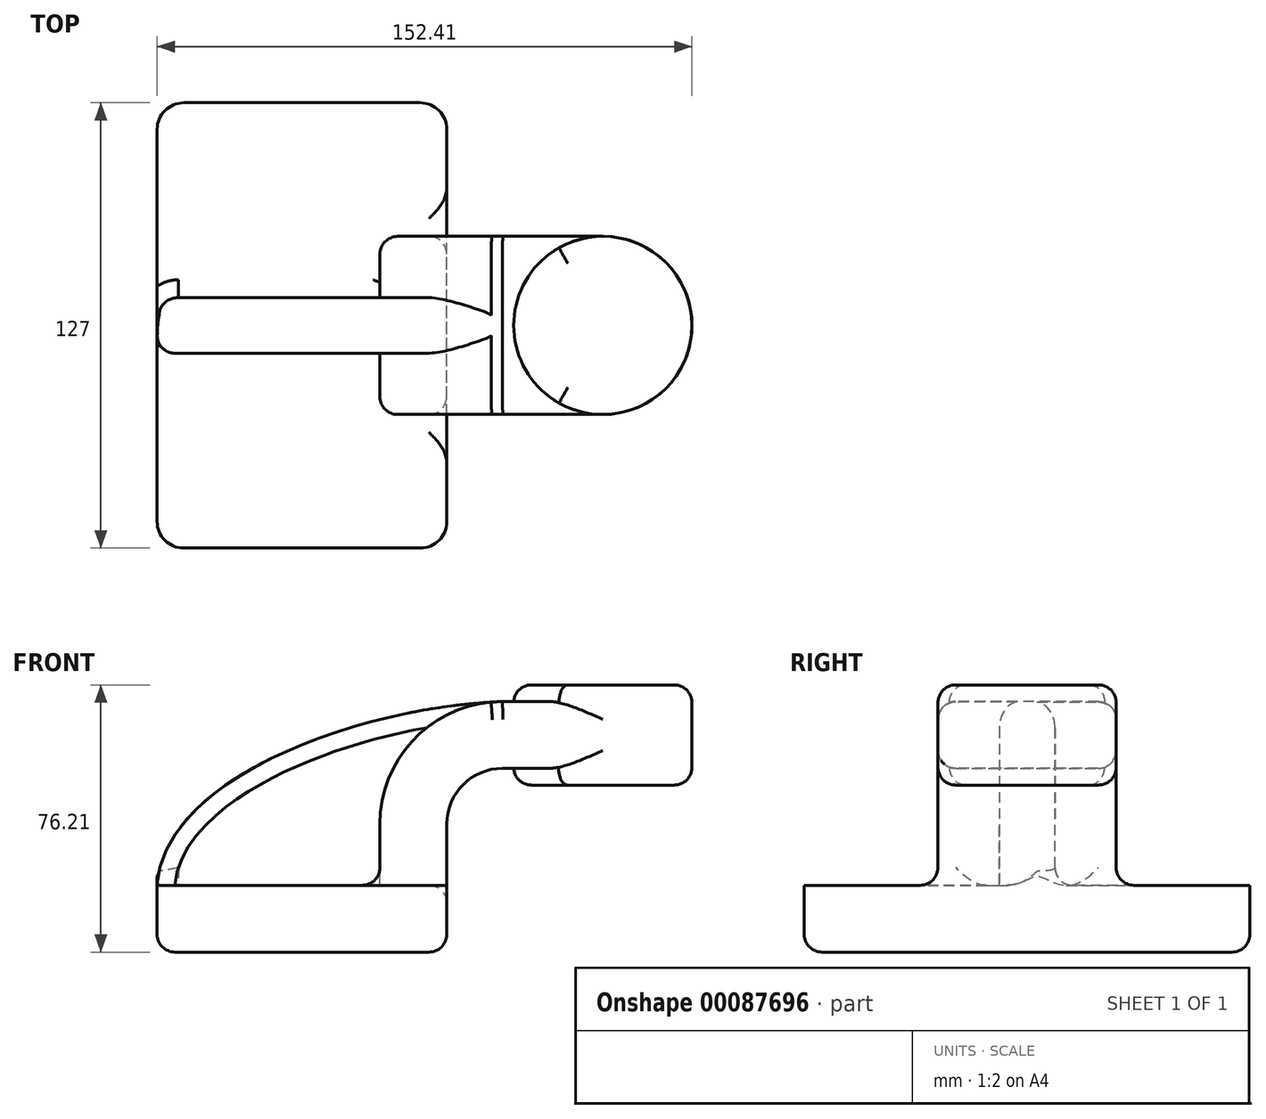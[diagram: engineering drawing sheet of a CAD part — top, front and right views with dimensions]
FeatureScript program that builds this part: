
annotation { "Feature Type Name" : "Feature", "Feature Type Description" : "" }
export const myFeature = defineFeature(function(context is Context, id is Id, definition is map)
    precondition{}
    {
        {
            var Q0;
            Q0=qCreatedBy(makeId("Front.planeOp"),FACE);
            var sketch = newSketch(context, id + "F0", { "sketchPlane" : qUnion([Q0])});
            skLineSegment(sketch, "E0.rect.bottom", {"start": v(-41.28, 9.52) * mm, "end": v(41.28, 9.52) * mm});
            skLineSegment(sketch, "E0.rect.top", {"start": v(-41.28, -9.52) * mm, "end": v(41.28, -9.52) * mm});
            skLineSegment(sketch, "E0.rect.left", {"start": v(-41.28, 9.52) * mm, "end": v(-41.28, -9.52) * mm});
            skLineSegment(sketch, "E0.rect.right", {"start": v(41.28, 9.52) * mm, "end": v(41.28, -9.52) * mm});
            skPoint(sketch, "E0.rect.middle", {"position": v(0, 0) * mm});
            skLineSegment(sketch, "E1", {"start": v(41.28, 9.52) * mm, "end": v(41.28, 27) * mm});
            skArc(sketch, "E2", {"start": v(41.28, 27) * mm, "mid": v(45.92, 38.23) * mm, "end": v(57.15, 42.88) * mm});
            skLineSegment(sketch, "E3", {"start": v(57.15, 42.88) * mm, "end": v(85.72, 42.88) * mm});
            skLineSegment(sketch, "E4.rect.bottom", {"start": v(60.32, 38.1) * mm, "end": v(111.12, 38.1) * mm});
            skLineSegment(sketch, "E4.rect.top", {"start": v(60.32, 66.68) * mm, "end": v(111.12, 66.68) * mm});
            skLineSegment(sketch, "E4.rect.left", {"start": v(60.32, 38.1) * mm, "end": v(60.32, 66.68) * mm});
            skLineSegment(sketch, "E4.rect.right", {"start": v(111.13, 38.1) * mm, "end": v(111.12, 66.68) * mm});
            skPoint(sketch, "E4.rect.middle", {"position": v(85.72, 52.39) * mm});
            skLineSegment(sketch, "E5.0", {"start": v(57.15, 61.93) * mm, "end": v(85.72, 61.93) * mm});
            skArc(sketch, "E5.1", {"start": v(22.23, 27) * mm, "mid": v(32.45, 51.7) * mm, "end": v(57.15, 61.93) * mm});
            skLineSegment(sketch, "E5.2", {"start": v(22.23, 9.52) * mm, "end": v(22.23, 27) * mm});
            skLineSegment(sketch, "E6", {"start": v(85.72, 38.1) * mm, "end": v(85.72, 66.68) * mm});
            skFitSpline(sketch, "E7", {"points": [v(-41.28, 9.53) * mm, v(57.15, 61.93) * mm], "startDerivative": vector(5.2, 92.34) * mm, "endDerivative": vector(120.92, 4.22) * mm});
            skSolve(sketch);
        }
        {
            var Q0;
            Q0=makeQuery(id+"F0.imprint","IMPRINT",FACE,{"disambiguationData":[TD([[makeQuery(id+"F0.imprint","IMPRINT",EDGE,{"derivedFrom":sQuery(id+"F0.wireOp",EDGE,"E0.rect.top")}),1.0]])]});
            extrude(context, id + "F1", {"entities" : qUnion([Q0]), "endBound" : BoundingType.SYMMETRIC, "depth" : 127 * mm});
        }
        {
            var Q0;
            {var subQ9=sQuery(id+"F0.wireOp",EDGE,"E1");Q0=makeQuery(id+"F0.imprint","IMPRINT",FACE,{"disambiguationData":[TD([[makeQuery(id+"F0.imprint","IMPRINT",EDGE,{"derivedFrom":subQ9}),1.0]])]});}
            var Q1;
            {var subQ0=sQuery(id+"F0.wireOp",EDGE,"E6");var subQ1=sQuery(id+"F0.wireOp",EDGE,"E3");var subQ2=makeQuery(id+"F0.imprint","INTERSECT",VERTEX,{"derivedFrom":[subQ1,subQ0]});Q1=makeQuery(id+"F0.imprint","IMPRINT",FACE,{"disambiguationData":[TD([[makeQuery(id+"F0.imprint","IMPRINT",EDGE,{"disambiguationData":[TD([[subQ2,1.0]])],"derivedFrom":subQ1}),1.0]])]});}
            extrude(context, id + "F2", {"entities" : qUnion([Q0, Q1]), "operationType" : NewBodyOperationType.ADD, "endBound" : BoundingType.SYMMETRIC, "depth" : 50.8 * mm});
        }
        {
            var Q0;
            {var subQ3=sQuery(id+"F0.wireOp",EDGE,"E5.2");Q0=makeQuery(id+"F0.imprint","IMPRINT",FACE,{"disambiguationData":[TD([[makeQuery(id+"F0.imprint","IMPRINT",EDGE,{"derivedFrom":subQ3}),1.0]])]});}
            extrude(context, id + "F3", {"entities" : qUnion([Q0]), "operationType" : NewBodyOperationType.ADD, "endBound" : BoundingType.SYMMETRIC, "depth" : 15.88 * mm});
        }
        {
            var Q0;
            {var subQ5=sQuery(id+"F0.wireOp",EDGE,"E4.rect.right");Q0=makeQuery(id+"F0.imprint","IMPRINT",FACE,{"disambiguationData":[TD([[makeQuery(id+"F0.imprint","IMPRINT",EDGE,{"derivedFrom":subQ5}),1.0]])]});}
            var Q1;
            Q1=sQuery(id+"F0.wireOp",EDGE,"E6");
            revolve(context, id + "F4", {"operationType" : NewBodyOperationType.ADD, "entities" : qUnion([Q0]), "axis" : qUnion([Q1]), "revolveType" : RevolveType.FULL});
        }
        {
            var Q0;
            Q0=makeQuery(id+"F1.opExtrude","CAP_EDGE",EDGE,{"disambiguationData":[OSD([sQuery(id+"F0.wireOp",EDGE,"E0.rect.right")])],"isStart":false});
            var Q1;
            Q1=makeQuery(id+"F1.opExtrude","CAP_EDGE",EDGE,{"disambiguationData":[OSD([sQuery(id+"F0.wireOp",EDGE,"E0.rect.left")])],"isStart":false});
            var Q2;
            Q2=makeQuery(id+"F1.opExtrude","CAP_EDGE",EDGE,{"disambiguationData":[OSD([sQuery(id+"F0.wireOp",EDGE,"E0.rect.right")])],"isStart":true});
            var Q3;
            Q3=makeQuery(id+"F1.opExtrude","CAP_EDGE",EDGE,{"disambiguationData":[OSD([sQuery(id+"F0.wireOp",EDGE,"E0.rect.left")])],"isStart":true});
            fillet(context, id + "F5", {"entities" : qUnion([Q0, Q1, Q2, Q3]), "radius" : 7.62 * mm, "tangentPropagation" : true, "allowEdgeOverflow" : false});
        }
        {
            var Q0;
            Q0=makeQuery(id+"F3.opExtrude","CAP_EDGE",EDGE,{"disambiguationData":[OSD([sQuery(id+"F0.wireOp",EDGE,"E7")])],"isStart":false});
            var Q1;
            Q1=makeQuery(id+"F3.opExtrude","CAP_EDGE",EDGE,{"disambiguationData":[OSD([sQuery(id+"F0.wireOp",EDGE,"E7")])],"isStart":true});
            fillet(context, id + "F6", {"entities" : qUnion([Q0, Q1]), "radius" : 5.08 * mm, "tangentPropagation" : true, "allowEdgeOverflow" : false});
        }
        {
            var Q0;
            Q0=makeQuery(id+"F2.opExtrude","CAP_FACE",FACE,{"disambiguationData":[OSD([sQuery(id+"F0.wireOp",EDGE,"E0.rect.bottom"),sQuery(id+"F0.wireOp",EDGE,"E1"),sQuery(id+"F0.wireOp",EDGE,"E2"),sQuery(id+"F0.wireOp",EDGE,"E3"),sQuery(id+"F0.wireOp",EDGE,"E5.0"),sQuery(id+"F0.wireOp",EDGE,"E5.1"),sQuery(id+"F0.wireOp",EDGE,"E5.2"),sQuery(id+"F0.wireOp",EDGE,"E6"),sQuery(id+"F0.wireOp",EDGE,"E7")])],"isStart":true});
            var Q1;
            Q1=makeQuery(id+"F2.opExtrude","CAP_FACE",FACE,{"disambiguationData":[OSD([sQuery(id+"F0.wireOp",EDGE,"E0.rect.bottom"),sQuery(id+"F0.wireOp",EDGE,"E1"),sQuery(id+"F0.wireOp",EDGE,"E2"),sQuery(id+"F0.wireOp",EDGE,"E3"),sQuery(id+"F0.wireOp",EDGE,"E5.0"),sQuery(id+"F0.wireOp",EDGE,"E5.1"),sQuery(id+"F0.wireOp",EDGE,"E5.2"),sQuery(id+"F0.wireOp",EDGE,"E6"),sQuery(id+"F0.wireOp",EDGE,"E7")])],"isStart":false});
            fillet(context, id + "F7", {"entities" : qUnion([Q0, Q1]), "radius" : 5.08 * mm, "tangentPropagation" : true, "allowEdgeOverflow" : false});
        }
        {
            var Q0;
            Q0=makeQuery(id+"F4.opRevolve","SWEPT_FACE",FACE,{"disambiguationData":[OSD([sQuery(id+"F0.wireOp",EDGE,"E4.rect.top")])]});
            var Q1;
            Q1=makeQuery(id+"F4.opRevolve","SWEPT_FACE",FACE,{"disambiguationData":[OSD([sQuery(id+"F0.wireOp",EDGE,"E4.rect.bottom")])]});
            fillet(context, id + "F8", {"entities" : qUnion([Q0, Q1]), "radius" : 5.08 * mm, "tangentPropagation" : true, "allowEdgeOverflow" : false});
        }
        {
            var Q0;
            Q0=makeQuery(id+"F1.opExtrude","SWEPT_FACE",FACE,{"disambiguationData":[OSD([sQuery(id+"F0.wireOp",EDGE,"E0.rect.top")])]});
            fillet(context, id + "F9", {"entities" : qUnion([Q0]), "radius" : 5.08 * mm, "tangentPropagation" : true, "allowEdgeOverflow" : false});
        }
        {
            var Q0;
            Q0=makeQuery(id+"F3.opExtrude","CAP_EDGE",EDGE,{"disambiguationData":[OSD([sQuery(id+"F0.wireOp",EDGE,"E0.rect.bottom")])],"isStart":false});
            var Q1;
            Q1=makeQuery(id+"F3.opExtrude","CAP_EDGE",EDGE,{"disambiguationData":[OSD([sQuery(id+"F0.wireOp",EDGE,"E0.rect.bottom")])],"isStart":true});
            fillet(context, id + "F10", {"entities" : qUnion([Q0, Q1]), "radius" : 5.08 * mm, "tangentPropagation" : true, "allowEdgeOverflow" : false});
        }
    });
